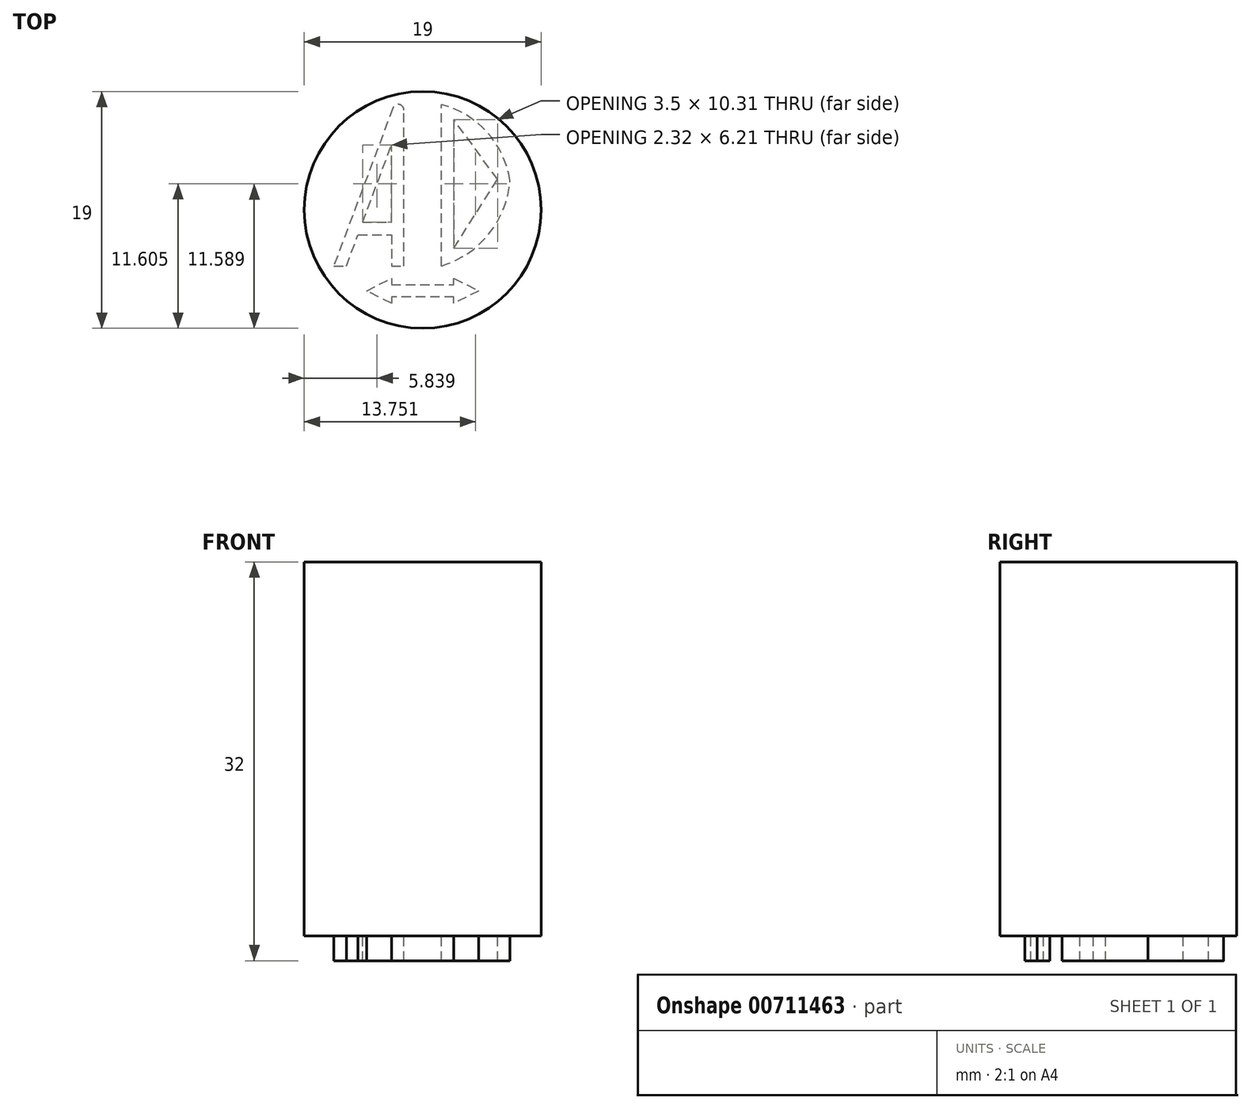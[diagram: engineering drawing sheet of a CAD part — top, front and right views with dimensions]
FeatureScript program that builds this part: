
annotation { "Feature Type Name" : "Feature", "Feature Type Description" : "" }
export const myFeature = defineFeature(function(context is Context, id is Id, definition is map)
    precondition{}
    {
        {
            var Q0;
            Q0=qCreatedBy(makeId("Top.planeOp"),FACE);
            var sketch = newSketch(context, id + "F0", { "sketchPlane" : qUnion([Q0])});
            skCircle(sketch, "E0", {"center": v(0, 0) * mm, "radius": 9.5 * mm});
            skLineSegment(sketch, "E1", {"start": v(-1.5, -4.5) * mm, "end": v(-1.5, 8) * mm});
            skLineSegment(sketch, "E2", {"start": v(-2.4, 8.16) * mm, "end": v(-7.13, -4.5) * mm});
            skLineSegment(sketch, "E3", {"start": v(-7.13, -4.5) * mm, "end": v(-6.13, -4.5) * mm});
            skLineSegment(sketch, "E4", {"start": v(-6.13, -4.5) * mm, "end": v(-5.2, -2) * mm});
            skLineSegment(sketch, "E5", {"start": v(-5.2, -2) * mm, "end": v(-2.5, -2) * mm});
            skLineSegment(sketch, "E6", {"start": v(-2.5, -2) * mm, "end": v(-2.5, -4.5) * mm});
            skLineSegment(sketch, "E7", {"start": v(-2.5, -4.5) * mm, "end": v(-1.5, -4.5) * mm});
            skLineSegment(sketch, "E8", {"start": v(-4.82, -1) * mm, "end": v(-2.5, 5.21) * mm});
            skLineSegment(sketch, "E9", {"start": v(-2.5, -1) * mm, "end": v(-2.5, 5.21) * mm});
            skLineSegment(sketch, "E10", {"start": v(-4.82, -1) * mm, "end": v(-2.5, -1) * mm});
            skPoint(sketch, "E11.visualSharp", {"position": v(-1.5, 10.56) * mm});
            skArc(sketch, "E11.filletArc", {"start": v(-1.5, 8) * mm, "mid": v(-1.88, 8.46) * mm, "end": v(-2.4, 8.16) * mm});
            skLineSegment(sketch, "E12", {"start": v(1.5, -4.5) * mm, "end": v(1.5, 8.46) * mm});
            skPoint(sketch, "E12.endSnap0", {"position": v(-1.88, 8.46) * mm});
            skArc(sketch, "E13", {"start": v(7, 2.38) * mm, "mid": v(5.15, 6.24) * mm, "end": v(1.5, 8.46) * mm});
            skArc(sketch, "E14", {"start": v(1.5, -4.5) * mm, "mid": v(5.32, -1.91) * mm, "end": v(7, 2.38) * mm});
            skLineSegment(sketch, "E15", {"start": v(2.5, 7.25) * mm, "end": v(2.5, -3.07) * mm});
            skLineSegment(sketch, "E16", {"start": v(2.5, -3.07) * mm, "end": v(6, 2.45) * mm});
            skLineSegment(sketch, "E17", {"start": v(6, 2.45) * mm, "end": v(2.5, 7.25) * mm});
            skLineSegment(sketch, "E18", {"start": v(-2.5, -6) * mm, "end": v(2.5, -6) * mm});
            skLineSegment(sketch, "E19", {"start": v(2.5, -6) * mm, "end": v(2.5, -5.5) * mm});
            skLineSegment(sketch, "E20", {"start": v(2.5, -5.5) * mm, "end": v(4.5, -6.5) * mm});
            skLineSegment(sketch, "E21", {"start": v(4.5, -6.5) * mm, "end": v(2.5, -7.5) * mm});
            skLineSegment(sketch, "E22", {"start": v(2.5, -7.5) * mm, "end": v(2.5, -7) * mm});
            skLineSegment(sketch, "E23", {"start": v(2.5, -7) * mm, "end": v(-2.5, -7) * mm});
            skLineSegment(sketch, "E24", {"start": v(-2.5, -7) * mm, "end": v(-2.5, -7.5) * mm});
            skLineSegment(sketch, "E25", {"start": v(-2.5, -7.5) * mm, "end": v(-4.5, -6.5) * mm});
            skLineSegment(sketch, "E26", {"start": v(-4.5, -6.5) * mm, "end": v(-2.5, -5.5) * mm});
            skLineSegment(sketch, "E27", {"start": v(-2.5, -5.5) * mm, "end": v(-2.5, -6) * mm});
            skSolve(sketch);
        }
        {
            var Q0;
            Q0=makeQuery(id+"F0.imprint","IMPRINT",FACE,{"disambiguationData":[TD([[makeQuery(id+"F0.imprint","IMPRINT",EDGE,{"derivedFrom":sQuery(id+"F0.wireOp",EDGE,"E1")}),1.0]])]});
            var Q1;
            Q1=makeQuery(id+"F0.imprint","IMPRINT",FACE,{"disambiguationData":[TD([[makeQuery(id+"F0.imprint","IMPRINT",EDGE,{"derivedFrom":sQuery(id+"F0.wireOp",EDGE,"E12")}),-1.0]])]});
            var Q2;
            Q2=makeQuery(id+"F0.imprint","IMPRINT",FACE,{"disambiguationData":[TD([[makeQuery(id+"F0.imprint","IMPRINT",EDGE,{"derivedFrom":sQuery(id+"F0.wireOp",EDGE,"E18")}),-1.0]])]});
            extrude(context, id + "F1", {"entities" : qUnion([Q0, Q1, Q2]), "oppositeDirection" : true, "depth" : 2 * mm, "offsetDistance" : 25 * mm});
        }
        {
            var Q0;
            Q0=makeQuery(id+"F0.imprint","IMPRINT",FACE,{"disambiguationData":[TD([[makeQuery(id+"F0.imprint","IMPRINT",EDGE,{"derivedFrom":sQuery(id+"F0.wireOp",EDGE,"E0")}),1.0]])]});
            var Q1;
            Q1=makeQuery(id+"F0.imprint","IMPRINT",FACE,{"disambiguationData":[TD([[makeQuery(id+"F0.imprint","IMPRINT",EDGE,{"derivedFrom":sQuery(id+"F0.wireOp",EDGE,"E8")}),-1.0]])]});
            var Q2;
            Q2=makeQuery(id+"F0.imprint","IMPRINT",FACE,{"disambiguationData":[TD([[makeQuery(id+"F0.imprint","IMPRINT",EDGE,{"derivedFrom":sQuery(id+"F0.wireOp",EDGE,"E1")}),1.0]])]});
            var Q3;
            Q3=makeQuery(id+"F0.imprint","IMPRINT",FACE,{"disambiguationData":[TD([[makeQuery(id+"F0.imprint","IMPRINT",EDGE,{"derivedFrom":sQuery(id+"F0.wireOp",EDGE,"E15")}),1.0]])]});
            var Q4;
            Q4=makeQuery(id+"F0.imprint","IMPRINT",FACE,{"disambiguationData":[TD([[makeQuery(id+"F0.imprint","IMPRINT",EDGE,{"derivedFrom":sQuery(id+"F0.wireOp",EDGE,"E12")}),-1.0]])]});
            var Q5;
            Q5=makeQuery(id+"F0.imprint","IMPRINT",FACE,{"disambiguationData":[TD([[makeQuery(id+"F0.imprint","IMPRINT",EDGE,{"derivedFrom":sQuery(id+"F0.wireOp",EDGE,"E18")}),-1.0]])]});
            extrude(context, id + "F2", {"entities" : qUnion([Q0, Q1, Q2, Q3, Q4, Q5]), "depth" : 30 * mm, "offsetDistance" : 25 * mm});
        }
    });
